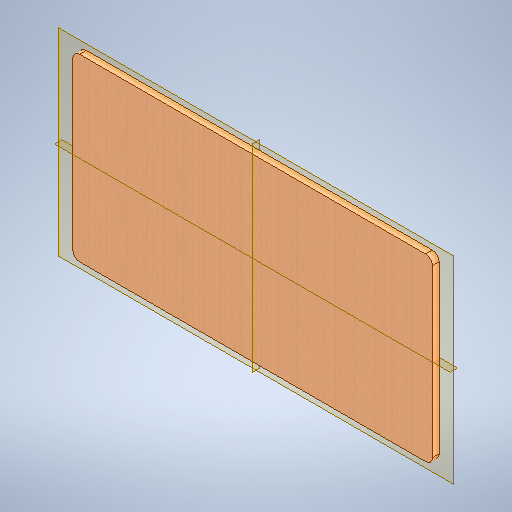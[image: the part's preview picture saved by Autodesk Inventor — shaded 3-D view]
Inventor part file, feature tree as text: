
AUTODESK INVENTOR PART (.ipt)
format: ipt  version: 2025.2 (Build 292293000, 293)  size: 330,240 bytes
history: native  units: mm
features: fillet x4, extrude x2, mirror x2, sketch x2, other x1
ambient origin geometry x8: Origin, YZ Plane, XZ Plane, XY Plane, X Axis, Y Axis, Z Axis, Center Point
bodies: Body1 (feature_tree)
feature tree (11):
  other  "Sólido1"
  extrude  "Extrusão1"  Depth=800.0mm
  fillet  "Arredondamento1"  Radius=30.0mm
  fillet  "Arredondamento2"  Radius=30.0mm
  fillet  "Arredondamento3"  Radius=30.0mm
  fillet  "Arredondamento4"  Radius=30.0mm
  extrude  "Extrusão2"  Depth=15.0mm
  mirror  "Espelhar1"
  mirror  "Espelhar2"
  sketch  "Esboço1"  dims[d0=1600.0mm d1=800.0mm d2=30.0mm d3=0.0mm d4=30.0mm d5=30.0mm d6=30.0mm]
  sketch  "Esboço3"  dims[d7=30.0mm d9=70.8mm d10=350.0mm d11=750.0mm d13=34.2mm d14=15.0mm d15=0.0mm]
